# Revit family: WCBrushHolder-WallMounted-Vitra-OriginSeries-A44894
name_source: partatom
category: Plumbing Fixtures
revit_build: Autodesk Revit 2017 (Build: 20160225_1515(x64)
units: mm (PartAtom-declared; Revit-internal decimal feet)

## family parameters
Cut with Voids When Loaded = No
Host = Face
OmniClass Number = 23.45.55.00
OmniClass Title = Sanitary Faucets, Wastes
Part Type = Normal
Room Calculation Point = No
Round Connector Dimension = Use Diameter
Shared = Yes

## types (4) — shared parameters
BIMobject category = Accessories
Brand = VitrA
CW Connection = No
Description = Origin Wc Brush Holder Wall
Design country = Turkey
HW Connection = No
IFC Classification = Sanitary Terminal
Main Material = Metal
Manufacturer = Vitra
Manufacturer name = Vitra
Masterformat 2014 Code = 10 28 13
Masterformat 2014 Description = Toilet Accessories
Mounting type = Wall Mounted
NBS Referans Code = 35-75-86
NBS Referans Description = Toilet Brush Holders
Nominal Depth (mm) = 80 mm
Nominal Height (mm) = 400 mm  [stored 1.31234 ft]
Nominal Width (mm) = 70 mm
OmniClass Code = 23-31 25 00
OmniClass Description = Toilet and Bath Specialties
Product Type = Wc Brush Holder Wall
Product certification = https://www.vitraglobal.com
Product data url = https://www.vitraglobal.com
Product family = Origin
Product group = Origin WC Brush Holder
Technical description = https://www.vitra.com.tr
UNSPSC Description = Plumbing Fixtures
URL = https://vitraglobal.com
Uniclass 1.4 Code = L7313
Uniclass 1.4 Description = Sanitary above ground pipes and fittings
Uniclass 2.0 Code = PR-35-75-86
Uniclass 2.0 Description = Toilet Brush Holders
Uniclass 2015 Code = PR_40_20_76_86
Uniclass 2015 Name = Toilet Brush Holders
Uniformat II Code = D2010
Uniformat II Description = Plumbing Fixtures
Vent Connection = No
Warranty Period (Year) = 5 Years
Waste Connection = No
Weight Net (kg) = 1.15
Youtube = https://www.youtube.com
zero-valued in all types: Default Elevation

## per-type parameters (varying)
| type | Article No. (default) | Coating Material | Color | Model | Product SKU |
| WCBrushHolder-Vitra-OriginSeries(Black)-A4489436 | A4489436 | Black | Black | A4489436 | A4489436 |
| WCBrushHolder-Vitra-OriginSeries(BrushedNickel)-A4489434 | A4489434 | Brushed Nickel | Brushed Nickel | A4489434 | A4489434 |
| WCBrushHolder-Vitra-OriginSeries(Copper)-A4489426 | A4489426 | Copper | Copper | A4489426 | A4489426 |
| WCBrushHolder-Vitra-OriginSeries(Chrome)-A44894 | A44894 | Chrome | Chrome | A44894 | A44894 |

note: [stored X ft] marks values corroborated as IEEE doubles in the binary element streams (Revit-internal decimal feet)

## geometry (parser evidence)
native form markers: Sweep x3
no freeform markers — native parametric forms only
